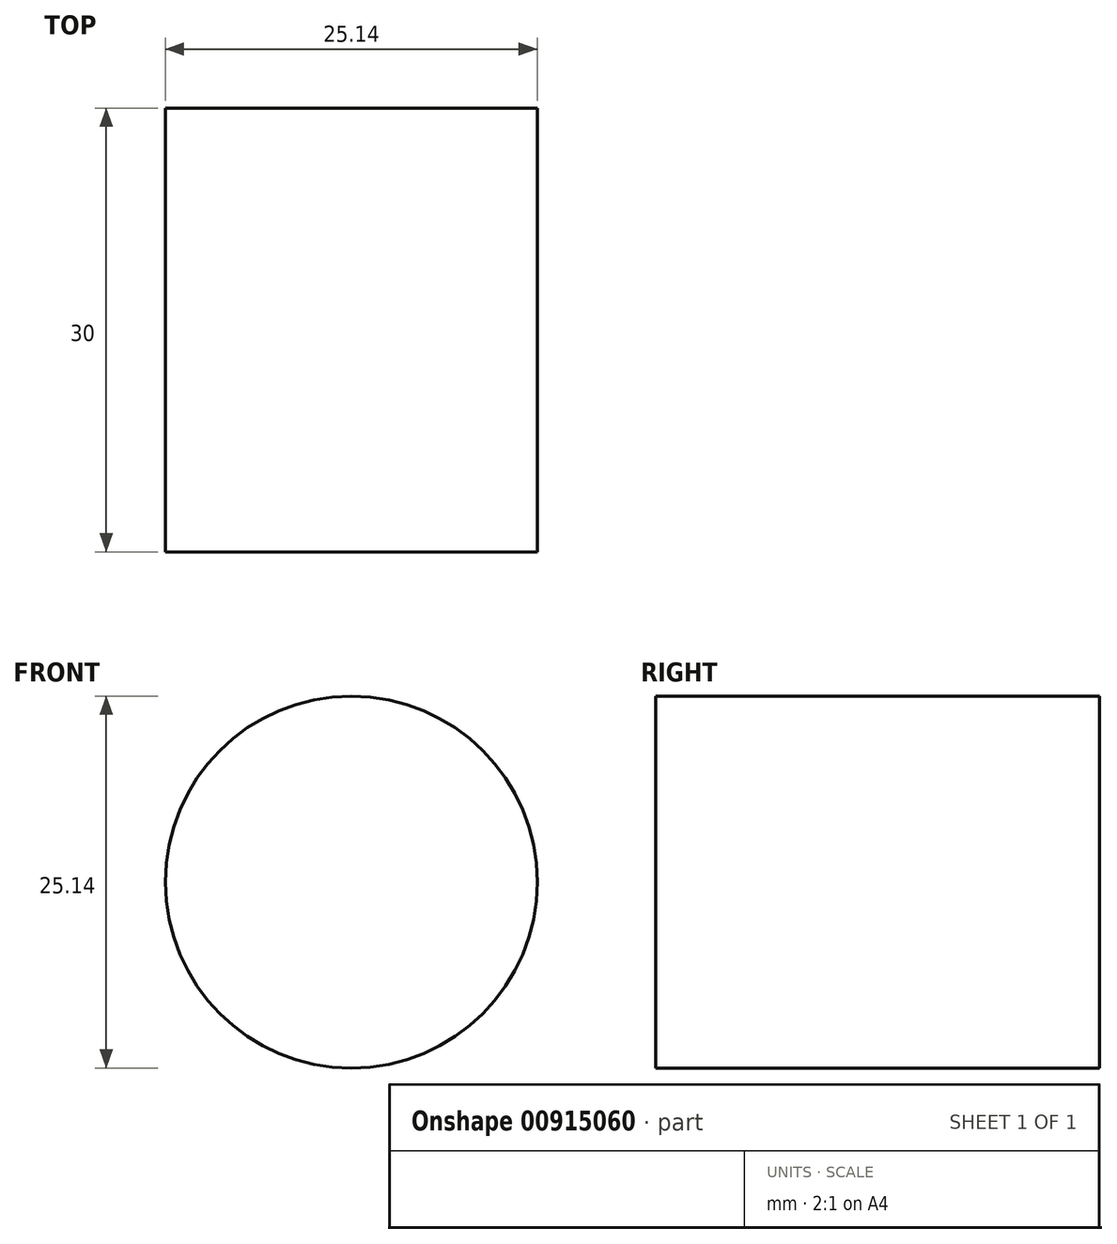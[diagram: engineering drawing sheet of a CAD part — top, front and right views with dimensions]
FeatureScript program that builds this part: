
annotation { "Feature Type Name" : "Feature", "Feature Type Description" : "" }
export const myFeature = defineFeature(function(context is Context, id is Id, definition is map)
    precondition{}
    {
        {
            var Q0;
            Q0=qCreatedBy(makeId("Front.planeOp"),FACE);
            var sketch = newSketch(context, id + "F0", { "sketchPlane" : qUnion([Q0])});
            skCircle(sketch, "E0", {"center": v(-51.84, 34.68) * mm, "radius": 12.57 * mm});
            skLineSegment(sketch, "E1", {"start": v(-51.84, 56.98) * mm, "end": v(-51.84, 10.25) * mm});
            skLineSegment(sketch, "E2", {"start": v(-51.84, 10.25) * mm, "end": v(-13.27, 10.25) * mm});
            skSolve(sketch);
        }
        {
            var Q0;
            Q0 = qSketchRegion(id + "F0", true);
            extrude(context, id + "F1", {"entities" : qUnion([Q0]), "depth" : 30 * mm, "offsetDistance" : 25 * mm});
        }
    });
